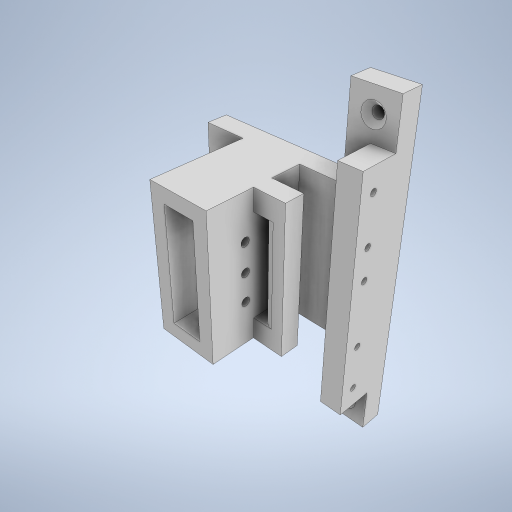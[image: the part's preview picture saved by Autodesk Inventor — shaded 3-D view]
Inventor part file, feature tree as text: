
AUTODESK INVENTOR PART (.ipt)
format: ipt  version: 2024 (Build 280153000, 153)  size: 462,336 bytes
history: native  units: mm
features: sketch x19, extrude x18, fillet x1, hole x1
ambient origin geometry x8: Origin, YZ Plane, XZ Plane, XY Plane, X Axis, Y Axis, Z Axis, Center Point
bodies: Solid1 (feature_tree)
feature tree (39):
  extrude  "Extrusion1"  Depth=45.2mm
  extrude  "Extrusion2"  Depth=7.0mm TaperAngle=0.0deg
  extrude  "Extrusion3"  Depth=7.0mm TaperAngle=0.0deg
  extrude  "Extrusion4"  Depth=10.0mm TaperAngle=0.0deg
  extrude  "Extrusion5"  Depth=20.0mm TaperAngle=0.0deg
  extrude  "Extrusion6"  Depth=54.2mm
  extrude  "Extrusion7"  Depth=45.2mm TaperAngle=0.0deg
  extrude  "Extrusion8"  Depth=20.0mm TaperAngle=0.0deg
  extrude  "Extrusion9"  Depth=15.0mm TaperAngle=0.0deg
  extrude  "Extrusion10"  TaperAngle=90.0deg  [1 undecoded]
  sketch  "Sketch11"  dims[d47=10.0mm d48=5.0mm]
  extrude  "Extrusion12"  Depth=5.0mm
  sketch  "Sketch13"  dims[d56=10.0mm d57=10.0mm]
  extrude  "Extrusion14"  Depth=7.0mm TaperAngle=0.0deg
  extrude  "Extrusion15"  Depth=10.0mm
  extrude  "Extrusion16"  Depth=4.5mm TaperAngle=0.0deg
  fillet  "Fillet2"  Radius=4.5mm
  extrude  "Extrusion17"  Depth=146.0mm
  extrude  "Extrusion18"  Depth=20.0mm
  extrude  "Extrusion19"  Depth=10.0mm
  extrude  "Extrusion20"  Depth=10.0mm
  hole  "Hole1"  [1 undecoded]
  sketch  "Sketch1"  dims[d0=54.2mm d1=45.2mm]
  sketch  "Sketch2"  dims[d2=15.3mm d3=0.0mm d4=7.0mm d5=0.0mm]
  sketch  "Sketch3"  dims[d6=7.0mm d7=0.0mm d8=7.0mm d9=0.0mm]
  sketch  "Sketch4"  dims[d10=7.0mm d11=0.0mm d12=10.0mm d13=0.0mm]
  sketch  "Sketch5"  dims[d14=10.0mm d15=20.0mm d16=0.0mm]
  sketch  "Sketch6"  dims[d17=15.2mm d18=54.2mm]
  sketch  "Sketch7"  dims[d19=45.2mm d20=0.0mm d34=39.25mm d35=0.0mm]
  sketch  "Sketch8"  dims[d36=10.0mm d37=20.0mm d38=0.0mm]
  sketch  "Sketch9"  dims[d42=9.0mm d43=15.0mm d44=0.0mm]
  sketch  "Sketch10"  dims[d45=10.0mm d46=90.0deg]
  sketch  "Sketch12"  dims[d52=7.0mm d53=0.0mm d54=7.0mm d55=0.0mm]
  sketch  "Sketch14"  dims[d58=90.0deg d59=9.75mm d60=0.0mm d61=4.5mm]
  sketch  "Sketch15"  dims[d62=10.0mm d63=146.0mm]
  sketch  "Sketch16"  dims[d64=20.0mm d65=0.0mm d66=20.0mm]
  sketch  "Sketch17"  dims[d67=20.0mm d68=10.0mm]
  sketch  "Sketch18"  dims[d69=20.0mm d70=0.0mm d71=10.0mm]
  sketch  "Sketch19"  dims[d72=21.0mm d73=10.0mm d74=21.0mm d75=14.0mm d76=3.0mm d77=3.0mm d78=3.0mm d79=3.0mm d80=3.0mm d81=5.0mm d82=20.0mm d83=0.0mm d84=1.5mm d85=0.0mm d86=10.0mm d87=10.0mm d88=15.0mm d89=15.0mm d90=5.0mm d91=6.0mm d92=10.0mm d93=2.0mm d94=90.0deg d95=8.0mm d96=20.594885mm]
note: 2 required parameter values undecoded (feature->parameter linkage not recoverable at this tier; creation-order binding heuristic only, values carry confidence <= 0.55)
